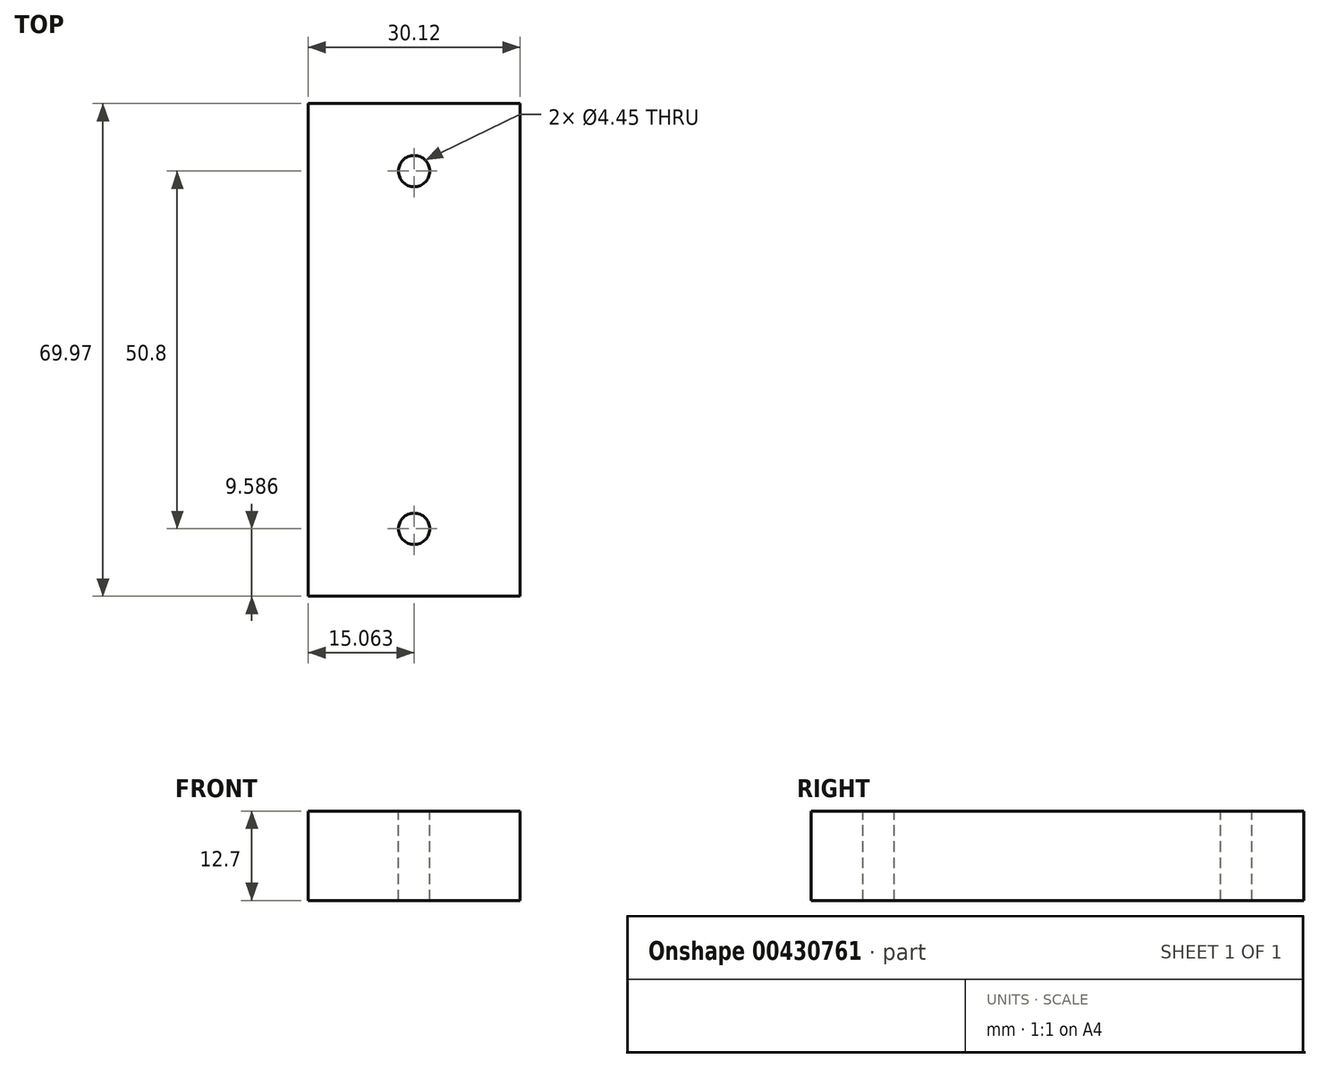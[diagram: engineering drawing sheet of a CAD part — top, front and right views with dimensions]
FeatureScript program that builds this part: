
annotation { "Feature Type Name" : "Feature", "Feature Type Description" : "" }
export const myFeature = defineFeature(function(context is Context, id is Id, definition is map)
    precondition{}
    {
        {
            var Q0;
            Q0=qCreatedBy(makeId("Top.planeOp"),FACE);
            var sketch = newSketch(context, id + "F0", { "sketchPlane" : qUnion([Q0])});
            skLineSegment(sketch, "E0.bottom", {"start": v(-40.24, 41.83) * mm, "end": v(-70.36, 41.83) * mm});
            skLineSegment(sketch, "E0.top", {"start": v(-40.24, -28.14) * mm, "end": v(-70.36, -28.14) * mm});
            skLineSegment(sketch, "E0.left", {"start": v(-40.24, 41.83) * mm, "end": v(-40.24, -28.14) * mm});
            skLineSegment(sketch, "E0.right", {"start": v(-70.36, 41.83) * mm, "end": v(-70.36, -28.14) * mm});
            skSolve(sketch);
        }
        {
            var Q0;
            Q0 = qSketchRegion(id + "F0", true);
            extrude(context, id + "F1", {"entities" : qUnion([Q0]), "depth" : 12.7 * mm});
        }
        {
            var Q0;
            Q0=makeQuery(id+"F1.opExtrude","CAP_FACE",FACE,{"disambiguationData":[OSD([sQuery(id+"F0.wireOp",EDGE,"E0.bottom"),sQuery(id+"F0.wireOp",EDGE,"E0.top"),sQuery(id+"F0.wireOp",EDGE,"E0.left"),sQuery(id+"F0.wireOp",EDGE,"E0.right")])],"isStart":false});
            var sketch = newSketch(context, id + "F2", { "sketchPlane" : qUnion([Q0])});
            skCircle(sketch, "E1", {"center": v(-55.3, -18.55) * mm, "radius": 2.22 * mm});
            skCircle(sketch, "E2", {"center": v(-55.3, 32.25) * mm, "radius": 2.22 * mm});
            skLineSegment(sketch, "E3", {"start": v(-55.3, 7.18) * mm, "end": v(-55.3, -44.29) * mm, "construction": true});
            skLineSegment(sketch, "E4", {"start": v(-89.14, 6.85) * mm, "end": v(-40.05, 6.85) * mm, "construction": true});
            skPoint(sketch, "E5", {"position": v(-55.3, -28.14) * mm});
            skSolve(sketch);
        }
        {
            var Q0;
            Q0 = qSketchRegion(id + "F2", true);
            extrude(context, id + "F3", {"entities" : qUnion([Q0]), "operationType" : NewBodyOperationType.REMOVE, "oppositeDirection" : true, "depth" : 25.4 * mm});
        }
    });
